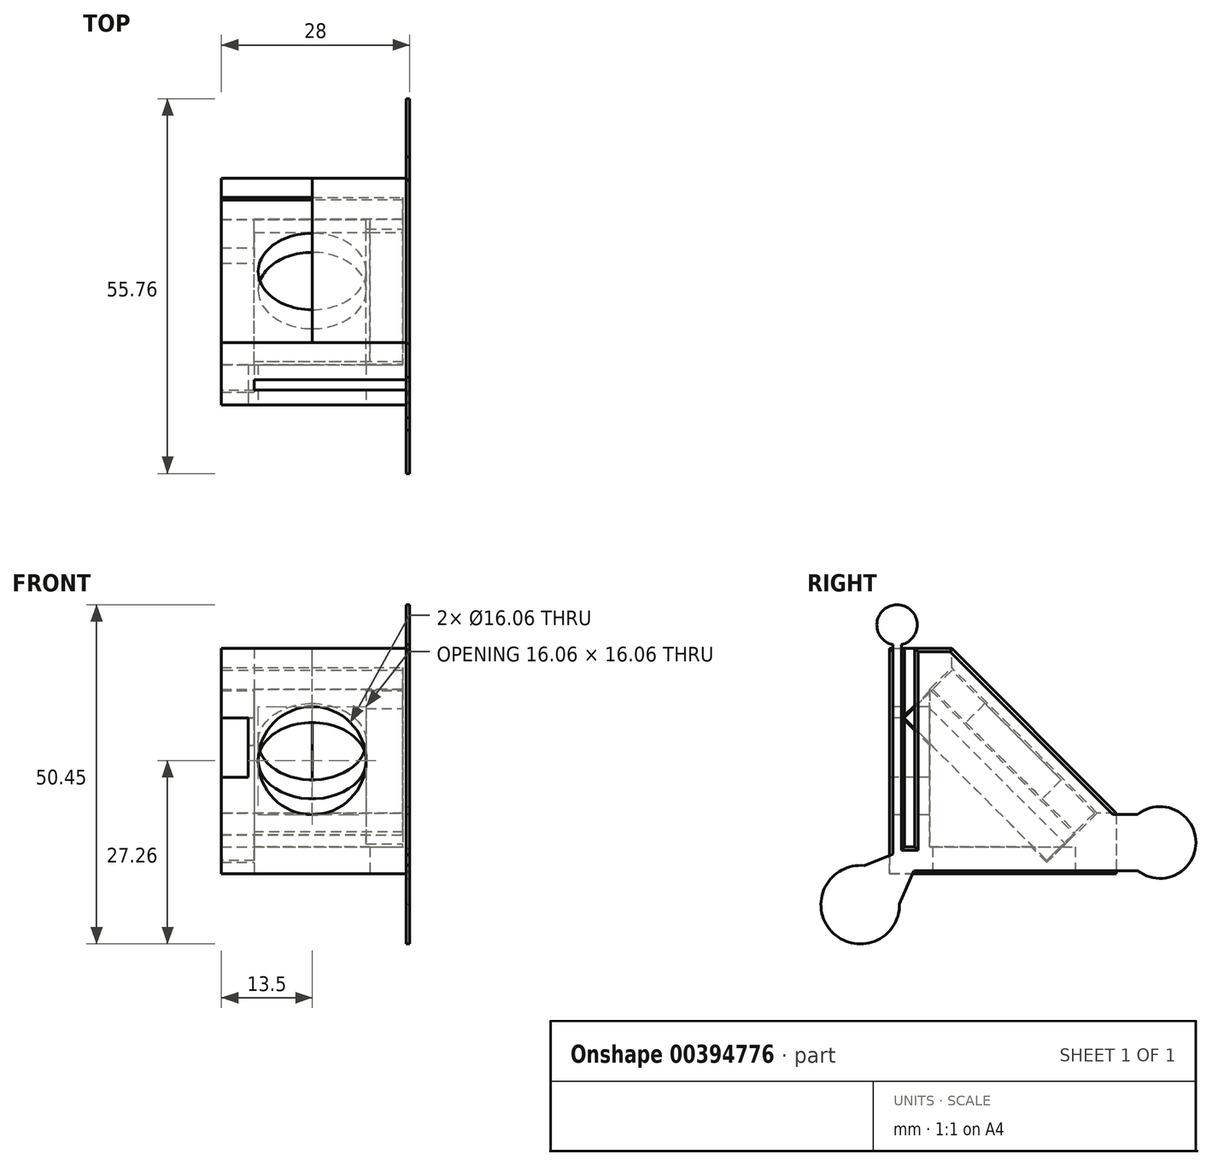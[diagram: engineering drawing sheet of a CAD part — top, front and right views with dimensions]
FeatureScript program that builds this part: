
annotation { "Feature Type Name" : "Feature", "Feature Type Description" : "" }
export const myFeature = defineFeature(function(context is Context, id is Id, definition is map)
    precondition{}
    {
        {
            var Q0;
            Q0=qCreatedBy(makeId("Top.planeOp"),FACE);
            var sketch = newSketch(context, id + "F0", { "sketchPlane" : qUnion([Q0])});
            skLineSegment(sketch, "E0", {"start": v(-77.13, 0) * mm, "end": v(74.23, 0) * mm, "construction": true});
            skSolve(sketch);
        }
        {
            var Q0;
            Q0=sQuery(id+"F0.wireOp",EDGE,"E0");
            cPlane(context, id + "F1", {"entities" : qUnion([Q0]), "cplaneType" : CPlaneType.LINE_ANGLE, "offset" : 25 * mm, "angle" : 45 * degree, "width" : 150 * mm, "height" : 150 * mm});
        }
        {
            var Q0;
            Q0=qCreatedBy(id+"F1.planeOp",FACE);
            var sketch = newSketch(context, id + "F2", { "sketchPlane" : qUnion([Q0])});
            skLineSegment(sketch, "E1.bottom", {"start": v(-13.5, -15) * mm, "end": v(13.5, -15) * mm});
            skLineSegment(sketch, "E1.top", {"start": v(-13.5, 15) * mm, "end": v(13.5, 15) * mm});
            skLineSegment(sketch, "E1.left", {"start": v(-13.5, -15) * mm, "end": v(-13.5, 15) * mm});
            skLineSegment(sketch, "E1.right", {"start": v(13.5, -15) * mm, "end": v(13.5, 15) * mm});
            skPoint(sketch, "E1.middle", {"position": v(0, 0) * mm});
            skLineSegment(sketch, "E2", {"start": v(13.5, 0) * mm, "end": v(8.6, 0) * mm, "construction": true});
            skPoint(sketch, "E2.endSnap0", {"position": v(13.5, 0) * mm});
            skLineSegment(sketch, "E3", {"start": v(-13.5, 0) * mm, "end": v(-8.03, 0) * mm, "construction": true});
            skPoint(sketch, "E3.endSnap0", {"position": v(-13.5, 0) * mm});
            skLineSegment(sketch, "E4", {"start": v(8.6, 15) * mm, "end": v(8.6, -15) * mm});
            skCircle(sketch, "E5", {"center": v(0, 0) * mm, "radius": 8.03 * mm});
            skSolve(sketch);
        }
        {
            var Q0;
            {var subQ1=sQuery(id+"F2.wireOp",EDGE,"E1.left");Q0=makeQuery(id+"F2.imprint","IMPRINT",FACE,{"disambiguationData":[TD([[makeQuery(id+"F2.imprint","IMPRINT",EDGE,{"derivedFrom":subQ1}),-1.0]])]});}
            var Q1;
            {var subQ0=sQuery(id+"F2.wireOp",EDGE,"E1.right");Q1=makeQuery(id+"F2.imprint","IMPRINT",FACE,{"disambiguationData":[TD([[makeQuery(id+"F2.imprint","IMPRINT",EDGE,{"derivedFrom":subQ0}),1.0]])]});}
            extrude(context, id + "F3", {"entities" : qUnion([Q0, Q1]), "depth" : 4 * mm});
        }
        {
            var Q0;
            {var subQ0=sQuery(id+"F2.wireOp",EDGE,"E1.right");Q0=makeQuery(id+"F2.imprint","IMPRINT",FACE,{"disambiguationData":[TD([[makeQuery(id+"F2.imprint","IMPRINT",EDGE,{"derivedFrom":subQ0}),1.0]])]});}
            extrude(context, id + "F4", {"entities" : qUnion([Q0]), "operationType" : NewBodyOperationType.ADD, "oppositeDirection" : true, "depth" : 6 * mm});
        }
        {
            var Q0;
            Q0=makeQuery(id+"F3.opExtrude","SWEPT_FACE",FACE,{"disambiguationData":[OSD([sQuery(id+"F2.wireOp",EDGE,"E1.left")])]});
            var sketch = newSketch(context, id + "F5", { "sketchPlane" : qUnion([Q0])});
            skLineSegment(sketch, "E6.0.0", {"start": v(-10.6, 10.6) * mm, "end": v(10.6, -10.6) * mm, "construction": true});
            skLineSegment(sketch, "E6.0.1", {"start": v(10.6, -10.6) * mm, "end": v(13.44, -7.78) * mm, "construction": true});
            skLineSegment(sketch, "E6.0.2", {"start": v(13.44, -7.78) * mm, "end": v(-7.78, 13.44) * mm, "construction": true});
            skLineSegment(sketch, "E6.0.3", {"start": v(-7.78, 13.44) * mm, "end": v(-10.6, 10.6) * mm, "construction": true});
            skLineSegment(sketch, "E7.0", {"start": v(13.86, -7.78) * mm, "end": v(-7.78, 13.86) * mm});
            skLineSegment(sketch, "E7.1", {"start": v(10.6, -11.03) * mm, "end": v(13.86, -7.78) * mm});
            skLineSegment(sketch, "E7.2", {"start": v(-11.03, 10.6) * mm, "end": v(10.6, -11.03) * mm});
            skLineSegment(sketch, "E7.3", {"start": v(-7.78, 13.86) * mm, "end": v(-11.03, 10.6) * mm});
            skLineSegment(sketch, "E8.0", {"start": v(16.69, -7.78) * mm, "end": v(-7.78, 16.69) * mm});
            skLineSegment(sketch, "E8.1", {"start": v(10.6, -13.86) * mm, "end": v(16.69, -7.78) * mm});
            skLineSegment(sketch, "E8.2", {"start": v(-13.86, 10.6) * mm, "end": v(10.6, -13.86) * mm});
            skLineSegment(sketch, "E8.3", {"start": v(-7.78, 16.69) * mm, "end": v(-13.86, 10.6) * mm});
            skLineSegment(sketch, "E9", {"start": v(-7.78, 16.69) * mm, "end": v(-13.86, 16.69) * mm});
            skPoint(sketch, "E10.0", {"position": v(6.36, -14.85) * mm});
            skLineSegment(sketch, "E11", {"start": v(10.6, -13.86) * mm, "end": v(10.6, -14.85) * mm, "construction": true});
            skLineSegment(sketch, "E12", {"start": v(-11.03, 10.6) * mm, "end": v(-17.03, 10.6) * mm, "construction": true});
            skLineSegment(sketch, "E13", {"start": v(-17.03, 10.6) * mm, "end": v(-17.03, 16.69) * mm});
            skLineSegment(sketch, "E14", {"start": v(-17.03, 16.69) * mm, "end": v(-13.86, 16.69) * mm});
            skLineSegment(sketch, "E15", {"start": v(-17.03, 10.6) * mm, "end": v(-17.03, -14.85) * mm});
            skLineSegment(sketch, "E16", {"start": v(0, -14.85) * mm, "end": v(0, -12.85) * mm, "construction": true});
            skLineSegment(sketch, "E17", {"start": v(-11.03, 10.6) * mm, "end": v(-11.03, -12.85) * mm});
            skLineSegment(sketch, "E18", {"start": v(-11.03, -12.85) * mm, "end": v(9.6, -12.85) * mm});
            skPoint(sketch, "E19.0", {"position": v(-14.85, 6.36) * mm});
            skLineSegment(sketch, "E20", {"start": v(6.36, -14.85) * mm, "end": v(6.36, -16.85) * mm, "construction": true});
            skLineSegment(sketch, "E21", {"start": v(-17.03, -14.85) * mm, "end": v(-17.03, -16.85) * mm});
            skLineSegment(sketch, "E22", {"start": v(-17.03, -16.85) * mm, "end": v(16.69, -16.85) * mm});
            skLineSegment(sketch, "E23", {"start": v(16.69, -16.85) * mm, "end": v(16.69, -7.78) * mm});
            skLineSegment(sketch, "E24.0", {"start": v(-14.85, 6.36) * mm, "end": v(-10.6, 10.6) * mm, "construction": true});
            skLineSegment(sketch, "E25.0", {"start": v(-14.85, 6.36) * mm, "end": v(6.36, -14.85) * mm, "construction": true});
            skLineSegment(sketch, "E26.0", {"start": v(6.36, -14.85) * mm, "end": v(10.6, -10.6) * mm, "construction": true});
            skLineSegment(sketch, "E27.1", {"start": v(-15.13, 6.36) * mm, "end": v(6.36, -15.13) * mm});
            skLineSegment(sketch, "E28", {"start": v(6.36, -15.13) * mm, "end": v(10.54, -10.96) * mm});
            skLineSegment(sketch, "E29", {"start": v(-15.13, 6.36) * mm, "end": v(-10.94, 10.51) * mm});
            skLineSegment(sketch, "E30", {"start": v(-7.78, 13.86) * mm, "end": v(-7.78, 16.69) * mm});
            skLineSegment(sketch, "E31", {"start": v(13.86, -7.78) * mm, "end": v(16.69, -7.78) * mm});
            skSolve(sketch);
        }
        {
            var Q0;
            Q0=makeQuery(id+"F5.imprint","IMPRINT",FACE,{"disambiguationData":[TD([[makeQuery(id+"F5.imprint","IMPRINT",EDGE,{"derivedFrom":sQuery(id+"F5.wireOp",EDGE,"E7.0")}),-1.0]])]});
            extrude(context, id + "F6", {"entities" : qUnion([Q0]), "oppositeDirection" : true, "depth" : 13.5 * mm});
        }
        {
            var Q0;
            {var subQ1=sQuery(id+"F5.wireOp",EDGE,"E7.3");Q0=makeQuery(id+"F5.imprint","IMPRINT",FACE,{"disambiguationData":[TD([[makeQuery(id+"F5.imprint","IMPRINT",EDGE,{"derivedFrom":subQ1}),-1.0]])]});}
            var Q1;
            {var subQ6=sQuery(id+"F5.wireOp",EDGE,"E8.1");Q1=makeQuery(id+"F5.imprint","IMPRINT",FACE,{"disambiguationData":[TD([[makeQuery(id+"F5.imprint","IMPRINT",EDGE,{"derivedFrom":subQ6}),-1.0]])]});}
            var Q2;
            {var subQ2=sQuery(id+"F5.wireOp",EDGE,"E7.1");Q2=makeQuery(id+"F5.imprint","IMPRINT",FACE,{"disambiguationData":[TD([[makeQuery(id+"F5.imprint","IMPRINT",EDGE,{"derivedFrom":subQ2}),-1.0]])]});}
            var Q3;
            {var subQ0=sQuery(id+"F5.wireOp",EDGE,"E18");var subQ1=sQuery(id+"F5.wireOp",EDGE,"E8.2");var subQ2=makeQuery(id+"F5.imprint","INTERSECT",VERTEX,{"derivedFrom":[subQ1,subQ0]});Q3=makeQuery(id+"F5.imprint","IMPRINT",FACE,{"disambiguationData":[TD([[makeQuery(id+"F5.imprint","IMPRINT",EDGE,{"disambiguationData":[TD([[subQ2,1.0]])],"derivedFrom":subQ1}),-1.0]])]});}
            var Q4;
            {var subQ0=sQuery(id+"F2.wireOp",EDGE,"E1.right");Q4=makeQuery(id+"F4.boolean.opBoolean","MERGE",FACE,{"derivedFrom":[makeQuery(id+"F3.opExtrude","SWEPT_FACE",FACE,{"disambiguationData":[OSD([subQ0])]}),makeQuery(id+"F4.opExtrude","SWEPT_FACE",FACE,{"disambiguationData":[OSD([subQ0])]})]});}
            extrude(context, id + "F7", {"entities" : qUnion([Q0, Q1, Q2, Q3]), "operationType" : NewBodyOperationType.ADD, "endBound" : BoundingType.UP_TO_SURFACE, "oppositeDirection" : true, "endBoundEntityFace" : qUnion([Q4]), "depth" : 25 * mm});
        }
        {
            var Q0;
            {var subQ0=sQuery(id+"F5.wireOp",EDGE,"E29");var subQ1=sQuery(id+"F5.wireOp",EDGE,"E8.2");var subQ2=makeQuery(id+"F5.imprint","INTERSECT",VERTEX,{"derivedFrom":[subQ1,subQ0]});Q0=makeQuery(id+"F5.imprint","IMPRINT",FACE,{"disambiguationData":[TD([[makeQuery(id+"F5.imprint","IMPRINT",EDGE,{"disambiguationData":[TD([[subQ2,-1.0]])],"derivedFrom":subQ1}),1.0]])]});}
            var Q1;
            {var subQ0=sQuery(id+"F5.wireOp",EDGE,"E29");var subQ1=sQuery(id+"F5.wireOp",EDGE,"E8.2");var subQ2=makeQuery(id+"F5.imprint","INTERSECT",VERTEX,{"derivedFrom":[subQ1,subQ0]});Q1=makeQuery(id+"F5.imprint","IMPRINT",FACE,{"disambiguationData":[TD([[makeQuery(id+"F5.imprint","IMPRINT",EDGE,{"disambiguationData":[TD([[subQ2,-1.0]])],"derivedFrom":subQ1}),-1.0]])]});}
            var Q2;
            {var subQ0=sQuery(id+"F5.wireOp",EDGE,"E27.1");var subQ1=sQuery(id+"F5.wireOp",EDGE,"E18");var subQ2=makeQuery(id+"F5.imprint","INTERSECT",VERTEX,{"derivedFrom":[subQ1,subQ0]});Q2=makeQuery(id+"F5.imprint","IMPRINT",FACE,{"disambiguationData":[TD([[makeQuery(id+"F5.imprint","IMPRINT",EDGE,{"disambiguationData":[TD([[subQ2,-1.0]])],"derivedFrom":subQ1}),-1.0]])]});}
            var Q3;
            Q3=makeQuery(id+"F4.opExtrude","SWEPT_FACE",FACE,{"disambiguationData":[OSD([sQuery(id+"F2.wireOp",EDGE,"E4")])]});
            extrude(context, id + "F8", {"entities" : qUnion([Q0, Q1, Q2]), "operationType" : NewBodyOperationType.ADD, "endBound" : BoundingType.UP_TO_SURFACE, "oppositeDirection" : true, "endBoundEntityFace" : qUnion([Q3]), "depth" : 25 * mm});
        }
        {
            var Q0;
            {var subQ5=sQuery(id+"F5.wireOp",EDGE,"E28");var subQ7=sQuery(id+"F5.wireOp",EDGE,"E7.2");var subQ8=makeQuery(id+"F5.imprint","INTERSECT",VERTEX,{"derivedFrom":[subQ7,subQ5]});Q0=makeQuery(id+"F5.imprint","IMPRINT",FACE,{"disambiguationData":[TD([[makeQuery(id+"F5.imprint","IMPRINT",EDGE,{"disambiguationData":[TD([[subQ8,1.0]])],"derivedFrom":subQ7}),-1.0]])]});}
            var Q1;
            Q1=sQuery(id+"F2.wireOp",VERTEX,"E3.end");
            extrude(context, id + "F9", {"entities" : qUnion([Q0]), "operationType" : NewBodyOperationType.ADD, "endBound" : BoundingType.UP_TO_VERTEX, "oppositeDirection" : true, "endBoundEntityVertex" : qUnion([Q1]), "depth" : 25 * mm});
        }
        {
            var Q0;
            Q0=makeQuery(id+"F7.opExtrude","SWEPT_FACE",FACE,{"disambiguationData":[OSD([sQuery(id+"F5.wireOp",EDGE,"E13"),sQuery(id+"F5.wireOp",EDGE,"E15"),sQuery(id+"F5.wireOp",EDGE,"E21")])]});
            var sketch = newSketch(context, id + "F10", { "sketchPlane" : qUnion([Q0])});
            skPoint(sketch, "E32.0", {"position": v(8.03, 0) * mm});
            skCircle(sketch, "E33", {"center": v(0, 0) * mm, "radius": 8.03 * mm});
            skSolve(sketch);
        }
        {
            var Q0;
            Q0=makeQuery(id+"F10.imprint","IMPRINT",FACE,{"disambiguationData":[TD([[makeQuery(id+"F10.imprint","IMPRINT",EDGE,{"derivedFrom":sQuery(id+"F10.wireOp",EDGE,"E33")}),1.0]])]});
            extrude(context, id + "F11", {"entities" : qUnion([Q0]), "operationType" : NewBodyOperationType.REMOVE, "oppositeDirection" : true, "depth" : 6 * mm});
        }
        {
            var Q0;
            {var subQ6=sQuery(id+"F5.wireOp",EDGE,"E8.1");Q0=makeQuery(id+"F5.imprint","IMPRINT",FACE,{"disambiguationData":[TD([[makeQuery(id+"F5.imprint","IMPRINT",EDGE,{"derivedFrom":subQ6}),-1.0]])]});}
            var sketch = newSketch(context, id + "F12", { "sketchPlane" : qUnion([Q0])});
            skPoint(sketch, "E34.0", {"position": v(-17.03, 16.69) * mm});
            skLineSegment(sketch, "E35", {"start": v(-17.03, 16.69) * mm, "end": v(-14.03, 16.69) * mm, "construction": true});
            skPoint(sketch, "E36.0", {"position": v(-11.03, -12.85) * mm});
            skLineSegment(sketch, "E37.bottom", {"start": v(-13.28, -12.85) * mm, "end": v(-14.78, -12.85) * mm});
            skLineSegment(sketch, "E37.left", {"start": v(-13.28, -12.85) * mm, "end": v(-13.28, 16.69) * mm});
            skLineSegment(sketch, "E37.right", {"start": v(-14.78, -12.85) * mm, "end": v(-14.78, 16.69) * mm});
            skPoint(sketch, "E37.middle", {"position": v(-14.03, 16.69) * mm});
            skLineSegment(sketch, "E38", {"start": v(-14.78, 16.69) * mm, "end": v(-13.28, 16.69) * mm});
            skSolve(sketch);
        }
        {
            var Q0;
            {var subQ0=sQuery(id+"F12.wireOp",EDGE,"E38");var subQ2=sQuery(id+"F12.wireOp",EDGE,"E37.right");var subQ3=makeQuery(id+"F12.imprint","INTERSECT",VERTEX,{"derivedFrom":[makeQuery(id+"F5.imprint","IMPRINT",EDGE,{"derivedFrom":sQuery(id+"F5.wireOp",EDGE,"E14")}),subQ2,subQ0]});Q0=makeQuery(id+"F12.imprint","IMPRINT",FACE,{"disambiguationData":[TD([[makeQuery(id+"F12.imprint","IMPRINT",EDGE,{"disambiguationData":[TD([[subQ3,-1.0]])],"derivedFrom":subQ0}),-1.0]])]});}
            var Q1;
            {var subQ0=sQuery(id+"F12.wireOp",EDGE,"E37.left");var subQ1=sQuery(id+"F5.wireOp",EDGE,"E8.3");var subQ5=makeQuery(id+"F5.imprint","IMPRINT",EDGE,{"derivedFrom":subQ1});var subQ6=makeQuery(id+"F12.imprint","INTERSECT",VERTEX,{"derivedFrom":[subQ5,subQ0]});Q1=makeQuery(id+"F12.imprint","IMPRINT",FACE,{"disambiguationData":[TD([[makeQuery(id+"F12.imprint","IMPRINT",EDGE,{"disambiguationData":[TD([[subQ6,1.0]])],"derivedFrom":subQ0}),1.0]])]});}
            var Q2;
            {var subQ0=sQuery(id+"F12.wireOp",EDGE,"E37.left");var subQ1=sQuery(id+"F5.wireOp",EDGE,"E29");var subQ2=sQuery(id+"F5.wireOp",EDGE,"E27.1");var subQ3=makeQuery(id+"F5.imprint","INTERSECT",VERTEX,{"derivedFrom":[subQ2,subQ1]});var subQ4=makeQuery(id+"F5.imprint","IMPRINT",EDGE,{"disambiguationData":[TD([[subQ3,-1.0]])],"derivedFrom":subQ2});var subQ5=makeQuery(id+"F12.imprint","INTERSECT",VERTEX,{"derivedFrom":[subQ4,subQ0]});Q2=makeQuery(id+"F12.imprint","IMPRINT",FACE,{"disambiguationData":[TD([[makeQuery(id+"F12.imprint","IMPRINT",EDGE,{"disambiguationData":[TD([[subQ5,-1.0]])],"derivedFrom":subQ0}),1.0]])]});}
            var Q3;
            {var subQ0=sQuery(id+"F12.wireOp",EDGE,"E37.bottom");Q3=makeQuery(id+"F12.imprint","IMPRINT",FACE,{"disambiguationData":[TD([[makeQuery(id+"F12.imprint","IMPRINT",EDGE,{"derivedFrom":subQ0}),-1.0]])]});}
            var Q4;
            Q4=makeQuery(id+"F4.opExtrude","SWEPT_FACE",FACE,{"disambiguationData":[OSD([sQuery(id+"F2.wireOp",EDGE,"E4")])]});
            extrude(context, id + "F13", {"entities" : qUnion([Q0, Q1, Q2, Q3]), "operationType" : NewBodyOperationType.REMOVE, "endBound" : BoundingType.UP_TO_SURFACE, "oppositeDirection" : true, "endBoundEntityFace" : qUnion([Q4]), "depth" : 25 * mm});
        }
        {
            var Q0;
            Q0=makeQuery(id+"F7.opExtrude","CAP_FACE",FACE,{"disambiguationData":[OSD([sQuery(id+"F5.wireOp",EDGE,"E7.1"),sQuery(id+"F5.wireOp",EDGE,"E7.2"),sQuery(id+"F5.wireOp",EDGE,"E7.3"),sQuery(id+"F5.wireOp",EDGE,"E9"),sQuery(id+"F5.wireOp",EDGE,"E13"),sQuery(id+"F5.wireOp",EDGE,"E14"),sQuery(id+"F5.wireOp",EDGE,"E15"),sQuery(id+"F5.wireOp",EDGE,"E17"),sQuery(id+"F5.wireOp",EDGE,"E18"),sQuery(id+"F5.wireOp",EDGE,"E21"),sQuery(id+"F5.wireOp",EDGE,"E22"),sQuery(id+"F5.wireOp",EDGE,"E23"),sQuery(id+"F5.wireOp",EDGE,"E27.1"),sQuery(id+"F5.wireOp",EDGE,"E28"),sQuery(id+"F5.wireOp",EDGE,"E29"),sQuery(id+"F5.wireOp",EDGE,"E30"),sQuery(id+"F5.wireOp",EDGE,"E31")])],"isStart":false});
            var sketch = newSketch(context, id + "F14", { "sketchPlane" : qUnion([Q0])});
            skLineSegment(sketch, "E39.0.0", {"start": v(11.03, 2.26) * mm, "end": v(11.03, -12.85) * mm, "construction": true});
            skLineSegment(sketch, "E39.0.1", {"start": v(11.03, -12.85) * mm, "end": v(-4.08, -12.85) * mm, "construction": true});
            skLineSegment(sketch, "E39.0.2", {"start": v(-4.08, -12.85) * mm, "end": v(-6.36, -15.13) * mm, "construction": true});
            skLineSegment(sketch, "E39.0.3", {"start": v(-6.36, -15.13) * mm, "end": v(-10.54, -10.96) * mm, "construction": true});
            skLineSegment(sketch, "E39.0.4", {"start": v(-10.54, -10.96) * mm, "end": v(-10.6, -11.03) * mm, "construction": true});
            skLineSegment(sketch, "E39.0.5", {"start": v(-10.6, -11.03) * mm, "end": v(-13.86, -7.78) * mm, "construction": true});
            skLineSegment(sketch, "E39.0.6", {"start": v(-13.86, -7.78) * mm, "end": v(-16.69, -7.78) * mm, "construction": true});
            skLineSegment(sketch, "E39.0.7", {"start": v(-16.69, -7.78) * mm, "end": v(-16.69, -16.85) * mm, "construction": true});
            skLineSegment(sketch, "E39.0.8", {"start": v(-16.69, -16.85) * mm, "end": v(17.03, -16.85) * mm, "construction": true});
            skLineSegment(sketch, "E39.0.9", {"start": v(17.03, -16.85) * mm, "end": v(17.03, 16.69) * mm, "construction": true});
            skLineSegment(sketch, "E39.0.10", {"start": v(17.03, 16.69) * mm, "end": v(7.78, 16.69) * mm, "construction": true});
            skLineSegment(sketch, "E39.0.11", {"start": v(7.78, 16.69) * mm, "end": v(7.78, 13.86) * mm, "construction": true});
            skLineSegment(sketch, "E39.0.12", {"start": v(7.78, 13.86) * mm, "end": v(11.03, 10.6) * mm, "construction": true});
            skLineSegment(sketch, "E39.0.13", {"start": v(11.03, 10.6) * mm, "end": v(11.03, 10.42) * mm, "construction": true});
            skLineSegment(sketch, "E39.0.14", {"start": v(11.03, 10.42) * mm, "end": v(15.13, 6.36) * mm, "construction": true});
            skLineSegment(sketch, "E39.0.15", {"start": v(15.13, 6.36) * mm, "end": v(11.03, 2.26) * mm, "construction": true});
            skLineSegment(sketch, "E40", {"start": v(15.13, 6.36) * mm, "end": v(17.03, 6.36) * mm});
            skLineSegment(sketch, "E41", {"start": v(15.13, 6.36) * mm, "end": v(11.03, 2.26) * mm});
            skLineSegment(sketch, "E42", {"start": v(11.03, 2.26) * mm, "end": v(11.03, -2.47) * mm});
            skLineSegment(sketch, "E43", {"start": v(11.03, -2.47) * mm, "end": v(17.03, -2.47) * mm});
            skLineSegment(sketch, "E44", {"start": v(17.03, -2.47) * mm, "end": v(17.03, 6.36) * mm});
            skSolve(sketch);
        }
        {
            var Q0;
            Q0=makeQuery(id+"F14.imprint","IMPRINT",FACE,{"disambiguationData":[TD([[makeQuery(id+"F14.imprint","IMPRINT",EDGE,{"derivedFrom":sQuery(id+"F14.wireOp",EDGE,"E40")}),-1.0]])]});
            extrude(context, id + "F15", {"entities" : qUnion([Q0]), "operationType" : NewBodyOperationType.REMOVE, "oppositeDirection" : true, "depth" : 4 * mm});
        }
        {
            var Q0;
            {var subQ0=sQuery(id+"F5.wireOp",EDGE,"E29");var subQ1=sQuery(id+"F5.wireOp",EDGE,"E8.2");var subQ2=makeQuery(id+"F5.imprint","INTERSECT",VERTEX,{"derivedFrom":[subQ1,subQ0]});Q0=makeQuery(id+"F5.imprint","IMPRINT",FACE,{"disambiguationData":[TD([[makeQuery(id+"F5.imprint","IMPRINT",EDGE,{"disambiguationData":[TD([[subQ2,-1.0]])],"derivedFrom":subQ1}),-1.0]])]});}
            var Q1;
            {var subQ1=sQuery(id+"F5.wireOp",EDGE,"E7.3");Q1=makeQuery(id+"F5.imprint","IMPRINT",FACE,{"disambiguationData":[TD([[makeQuery(id+"F5.imprint","IMPRINT",EDGE,{"derivedFrom":subQ1}),-1.0]])]});}
            var Q2;
            {var subQ6=sQuery(id+"F5.wireOp",EDGE,"E8.1");Q2=makeQuery(id+"F5.imprint","IMPRINT",FACE,{"disambiguationData":[TD([[makeQuery(id+"F5.imprint","IMPRINT",EDGE,{"derivedFrom":subQ6}),-1.0]])]});}
            var Q3;
            {var subQ0=sQuery(id+"F5.wireOp",EDGE,"E18");var subQ1=sQuery(id+"F5.wireOp",EDGE,"E17");var subQ2=makeQuery(id+"F5.imprint","INTERSECT",VERTEX,{"derivedFrom":[subQ1,subQ0]});Q3=makeQuery(id+"F5.imprint","IMPRINT",FACE,{"disambiguationData":[TD([[makeQuery(id+"F5.imprint","IMPRINT",EDGE,{"disambiguationData":[TD([[subQ2,1.0]])],"derivedFrom":subQ1}),1.0]])]});}
            var Q4;
            {var subQ0=sQuery(id+"F5.wireOp",EDGE,"E29");var subQ1=sQuery(id+"F5.wireOp",EDGE,"E8.2");var subQ2=makeQuery(id+"F5.imprint","INTERSECT",VERTEX,{"derivedFrom":[subQ1,subQ0]});Q4=makeQuery(id+"F5.imprint","IMPRINT",FACE,{"disambiguationData":[TD([[makeQuery(id+"F5.imprint","IMPRINT",EDGE,{"disambiguationData":[TD([[subQ2,-1.0]])],"derivedFrom":subQ1}),1.0]])]});}
            var Q5;
            {var subQ1=sQuery(id+"F5.wireOp",EDGE,"E17");var subQ7=sQuery(id+"F5.wireOp",EDGE,"E8.2");var subQ8=makeQuery(id+"F5.imprint","INTERSECT",VERTEX,{"derivedFrom":[subQ7,subQ1]});Q5=makeQuery(id+"F5.imprint","IMPRINT",FACE,{"disambiguationData":[TD([[makeQuery(id+"F5.imprint","IMPRINT",EDGE,{"disambiguationData":[TD([[subQ8,-1.0]])],"derivedFrom":subQ7}),-1.0]])]});}
            var Q6;
            {var subQ5=sQuery(id+"F5.wireOp",EDGE,"E28");var subQ7=sQuery(id+"F5.wireOp",EDGE,"E7.2");var subQ8=makeQuery(id+"F5.imprint","INTERSECT",VERTEX,{"derivedFrom":[subQ7,subQ5]});Q6=makeQuery(id+"F5.imprint","IMPRINT",FACE,{"disambiguationData":[TD([[makeQuery(id+"F5.imprint","IMPRINT",EDGE,{"disambiguationData":[TD([[subQ8,1.0]])],"derivedFrom":subQ7}),-1.0]])]});}
            var Q7;
            Q7=makeQuery(id+"F5.imprint","IMPRINT",FACE,{"disambiguationData":[TD([[makeQuery(id+"F5.imprint","IMPRINT",EDGE,{"derivedFrom":sQuery(id+"F5.wireOp",EDGE,"E7.0")}),1.0]])]});
            var Q8;
            Q8=makeQuery(id+"F5.imprint","IMPRINT",FACE,{"disambiguationData":[TD([[makeQuery(id+"F5.imprint","IMPRINT",EDGE,{"derivedFrom":sQuery(id+"F5.wireOp",EDGE,"E7.0")}),-1.0]])]});
            var Q9;
            {var subQ0=sQuery(id+"F5.wireOp",EDGE,"E27.1");var subQ1=sQuery(id+"F5.wireOp",EDGE,"E18");var subQ2=makeQuery(id+"F5.imprint","INTERSECT",VERTEX,{"derivedFrom":[subQ1,subQ0]});Q9=makeQuery(id+"F5.imprint","IMPRINT",FACE,{"disambiguationData":[TD([[makeQuery(id+"F5.imprint","IMPRINT",EDGE,{"disambiguationData":[TD([[subQ2,-1.0]])],"derivedFrom":subQ1}),-1.0]])]});}
            var Q10;
            {var subQ2=sQuery(id+"F5.wireOp",EDGE,"E7.1");Q10=makeQuery(id+"F5.imprint","IMPRINT",FACE,{"disambiguationData":[TD([[makeQuery(id+"F5.imprint","IMPRINT",EDGE,{"derivedFrom":subQ2}),-1.0]])]});}
            var Q11;
            {var subQ0=sQuery(id+"F5.wireOp",EDGE,"E18");var subQ1=sQuery(id+"F5.wireOp",EDGE,"E8.2");var subQ2=makeQuery(id+"F5.imprint","INTERSECT",VERTEX,{"derivedFrom":[subQ1,subQ0]});Q11=makeQuery(id+"F5.imprint","IMPRINT",FACE,{"disambiguationData":[TD([[makeQuery(id+"F5.imprint","IMPRINT",EDGE,{"disambiguationData":[TD([[subQ2,1.0]])],"derivedFrom":subQ1}),-1.0]])]});}
            var Q12;
            {var subQ0=sQuery(id+"F2.wireOp",EDGE,"E1.left");Q12=makeQuery(id+"F5.imprint","IMPRINT",FACE,{"disambiguationData":[TD([[makeQuery(id+"F5.imprint","IMPRINT",EDGE,{"derivedFrom":makeQuery(id+"F3.opExtrude","CAP_EDGE",EDGE,{"disambiguationData":[OSD([subQ0])],"isStart":true})}),-1.0]])]});}
            var Q13;
            {var subQ1=sQuery(id+"F5.wireOp",EDGE,"E7.2");var subQ3=sQuery(id+"F5.wireOp",EDGE,"E29");var subQ4=makeQuery(id+"F5.imprint","INTERSECT",VERTEX,{"derivedFrom":[subQ1,subQ3]});Q13=makeQuery(id+"F5.imprint","IMPRINT",FACE,{"disambiguationData":[TD([[makeQuery(id+"F5.imprint","IMPRINT",EDGE,{"disambiguationData":[TD([[subQ4,1.0]])],"derivedFrom":subQ3}),1.0]])]});}
            extrude(context, id + "F16", {"entities" : qUnion([Q0, Q1, Q2, Q3, Q4, Q5, Q6, Q7, Q8, Q9, Q10, Q11, Q12, Q13]), "operationType" : NewBodyOperationType.ADD, "depth" : 1 * mm});
        }
        {
            var Q0;
            {var subQ0=sQuery(id+"F5.wireOp",EDGE,"E22");Q0=makeQuery(id+"F16.boolean.opBoolean","MERGE",FACE,{"derivedFrom":[makeQuery(id+"F7.opExtrude","SWEPT_FACE",FACE,{"disambiguationData":[OSD([subQ0])]}),makeQuery(id+"F16.opExtrude","SWEPT_FACE",FACE,{"disambiguationData":[OSD([subQ0])]})]});}
            var sketch = newSketch(context, id + "F17", { "sketchPlane" : qUnion([Q0])});
            skPoint(sketch, "E45.0", {"position": v(-8.6, -10.6) * mm});
            skLineSegment(sketch, "E46.bottom", {"start": v(-8.6, -10.6) * mm, "end": v(8.6, -10.6) * mm});
            skLineSegment(sketch, "E46.top", {"start": v(-8.6, 10.6) * mm, "end": v(8.6, 10.6) * mm});
            skLineSegment(sketch, "E46.left", {"start": v(-8.6, -10.6) * mm, "end": v(-8.6, 10.6) * mm});
            skLineSegment(sketch, "E46.right", {"start": v(8.6, -10.6) * mm, "end": v(8.6, 10.6) * mm});
            skPoint(sketch, "E46.middle", {"position": v(0, 0) * mm});
            skSolve(sketch);
        }
        {
            var Q0;
            Q0=makeQuery(id+"F17.imprint","IMPRINT",FACE,{"disambiguationData":[TD([[makeQuery(id+"F17.imprint","IMPRINT",EDGE,{"derivedFrom":sQuery(id+"F17.wireOp",EDGE,"E46.bottom")}),1.0]])]});
            var Q1;
            {var subQ0=sQuery(id+"F5.wireOp",EDGE,"E18");Q1=makeQuery(id+"F8.boolean.opBoolean","MERGE",FACE,{"derivedFrom":[makeQuery(id+"F7.opExtrude","SWEPT_FACE",FACE,{"disambiguationData":[OSD([subQ0])]}),makeQuery(id+"F8.opExtrude","SWEPT_FACE",FACE,{"disambiguationData":[OSD([subQ0])]})]});}
            extrude(context, id + "F18", {"entities" : qUnion([Q0]), "operationType" : NewBodyOperationType.REMOVE, "endBound" : BoundingType.UP_TO_SURFACE, "oppositeDirection" : true, "endBoundEntityFace" : qUnion([Q1]), "depth" : 25 * mm});
        }
        {
            var Q0;
            Q0=makeQuery(id+"F16.opExtrude","CAP_FACE",FACE,{"disambiguationData":[OSD([sQuery(id+"F5.wireOp",EDGE,"E8.0"),sQuery(id+"F5.wireOp",EDGE,"E9"),sQuery(id+"F5.wireOp",EDGE,"E13"),sQuery(id+"F5.wireOp",EDGE,"E14"),sQuery(id+"F5.wireOp",EDGE,"E15"),sQuery(id+"F5.wireOp",EDGE,"E21"),sQuery(id+"F5.wireOp",EDGE,"E22"),sQuery(id+"F5.wireOp",EDGE,"E23")])],"isStart":false});
            var sketch = newSketch(context, id + "F19", { "sketchPlane" : qUnion([Q0])});
            skLineSegment(sketch, "E47.0", {"start": v(-14.78, 16.69) * mm, "end": v(-13.28, 16.69) * mm});
            skLineSegment(sketch, "E48.0", {"start": v(-13.28, -12.85) * mm, "end": v(-13.28, 16.69) * mm});
            skLineSegment(sketch, "E49.0", {"start": v(-14.78, -12.85) * mm, "end": v(-14.78, 16.69) * mm});
            skLineSegment(sketch, "E50.0", {"start": v(-13.28, -12.85) * mm, "end": v(-14.78, -12.85) * mm});
            skSolve(sketch);
        }
        {
            var Q0;
            {var subQ0=sQuery(id+"F19.wireOp",EDGE,"E50.0");Q0=makeQuery(id+"F19.imprint","IMPRINT",FACE,{"disambiguationData":[TD([[makeQuery(id+"F19.imprint","IMPRINT",EDGE,{"derivedFrom":subQ0}),-1.0]])]});}
            var Q1;
            {var subQ0=sQuery(id+"F5.wireOp",EDGE,"E14");var subQ1=sQuery(id+"F5.wireOp",EDGE,"E9");Q1=makeQuery(id+"F16.boolean.opBoolean","SPLIT",FACE,{"disambiguationData":[TD([makeQuery(id+"F13.boolean.opBoolean","COPY",FACE,{"derivedFrom":makeQuery(id+"F13.opExtrude","SWEPT_FACE",FACE,{"disambiguationData":[OSD([sQuery(id+"F12.wireOp",EDGE,"E37.bottom")])]})})])],"derivedFrom":makeQuery(id+"F16.opExtrude","CAP_FACE",FACE,{"disambiguationData":[OSD([sQuery(id+"F5.wireOp",EDGE,"E8.0"),subQ1,sQuery(id+"F5.wireOp",EDGE,"E13"),subQ0,sQuery(id+"F5.wireOp",EDGE,"E15"),sQuery(id+"F5.wireOp",EDGE,"E21"),sQuery(id+"F5.wireOp",EDGE,"E22"),sQuery(id+"F5.wireOp",EDGE,"E23")])],"isStart":true})});}
            extrude(context, id + "F20", {"entities" : qUnion([Q0]), "operationType" : NewBodyOperationType.REMOVE, "endBound" : BoundingType.UP_TO_SURFACE, "oppositeDirection" : true, "endBoundEntityFace" : qUnion([Q1]), "depth" : 25 * mm});
        }
        {
            var Q0;
            Q0=makeQuery(id+"F16.opExtrude","CAP_FACE",FACE,{"disambiguationData":[OSD([sQuery(id+"F5.wireOp",EDGE,"E8.0"),sQuery(id+"F5.wireOp",EDGE,"E9"),sQuery(id+"F5.wireOp",EDGE,"E13"),sQuery(id+"F5.wireOp",EDGE,"E14"),sQuery(id+"F5.wireOp",EDGE,"E15"),sQuery(id+"F5.wireOp",EDGE,"E21"),sQuery(id+"F5.wireOp",EDGE,"E22"),sQuery(id+"F5.wireOp",EDGE,"E23")])],"isStart":false});
            chamfer(context, id + "F21", {"entities" : qUnion([Q0]), "width" : .5 * mm, "tangentPropagation" : true});
        }
        {
            var Q0;
            Q0=makeQuery(id+"F16.opExtrude","CAP_FACE",FACE,{"disambiguationData":[OSD([sQuery(id+"F5.wireOp",EDGE,"E8.0"),sQuery(id+"F5.wireOp",EDGE,"E9"),sQuery(id+"F5.wireOp",EDGE,"E13"),sQuery(id+"F5.wireOp",EDGE,"E14"),sQuery(id+"F5.wireOp",EDGE,"E15"),sQuery(id+"F5.wireOp",EDGE,"E21"),sQuery(id+"F5.wireOp",EDGE,"E22"),sQuery(id+"F5.wireOp",EDGE,"E23")])],"isStart":false});
            var sketch = newSketch(context, id + "F22", { "sketchPlane" : qUnion([Q0])});
            skLineSegment(sketch, "E51", {"start": v(-15.9, 16.19) * mm, "end": v(-15.9, 20.19) * mm, "construction": true});
            skCircle(sketch, "E52", {"center": v(-15.9, 20.19) * mm, "radius": 3 * mm});
            skLineSegment(sketch, "E53", {"start": v(-16.53, 16.19) * mm, "end": v(-16.53, 17.25) * mm});
            skLineSegment(sketch, "E54", {"start": v(-15.28, 16.19) * mm, "end": v(-15.28, 17.25) * mm});
            skLineSegment(sketch, "E55", {"start": v(-16.53, 16.19) * mm, "end": v(-15.28, 16.19) * mm});
            skLineSegment(sketch, "E56", {"start": v(16.19, -12.17) * mm, "end": v(23.19, -12.17) * mm, "construction": true});
            skCircle(sketch, "E57", {"center": v(23.19, -12.17) * mm, "radius": 5.34 * mm});
            skLineSegment(sketch, "E58", {"start": v(16.19, -16.35) * mm, "end": v(19.86, -16.35) * mm});
            skLineSegment(sketch, "E59", {"start": v(16.19, -7.99) * mm, "end": v(19.86, -7.99) * mm});
            skLineSegment(sketch, "E60", {"start": v(-16.53, -16.35) * mm, "end": v(-21.38, -21.42) * mm, "construction": true});
            skCircle(sketch, "E61", {"center": v(-21.38, -21.42) * mm, "radius": 5.84 * mm});
            skLineSegment(sketch, "E62", {"start": v(-13.43, -16.35) * mm, "end": v(-15.54, -21.32) * mm});
            skLineSegment(sketch, "E63", {"start": v(-16.53, -13.87) * mm, "end": v(-20.77, -15.61) * mm});
            skSolve(sketch);
        }
        {
            var Q0;
            {var subQ0=sQuery(id+"F22.wireOp",EDGE,"E52");var subQ1=makeQuery(id+"F22.imprint","INTERSECT",VERTEX,{"derivedFrom":[subQ0,sQuery(id+"F22.wireOp",EDGE,"E53")]});Q0=makeQuery(id+"F22.imprint","IMPRINT",FACE,{"disambiguationData":[TD([[makeQuery(id+"F22.imprint","IMPRINT",EDGE,{"disambiguationData":[TD([[subQ1,-1.0]])],"derivedFrom":subQ0}),1.0]])]});}
            var Q1;
            {var subQ0=sQuery(id+"F22.wireOp",EDGE,"E53");Q1=makeQuery(id+"F22.imprint","IMPRINT",FACE,{"disambiguationData":[TD([[makeQuery(id+"F22.imprint","IMPRINT",EDGE,{"derivedFrom":subQ0}),-1.0]])]});}
            var Q2;
            {var subQ0=sQuery(id+"F22.wireOp",EDGE,"E61");var subQ1=makeQuery(id+"F22.imprint","INTERSECT",VERTEX,{"derivedFrom":[subQ0,sQuery(id+"F22.wireOp",EDGE,"E62")]});Q2=makeQuery(id+"F22.imprint","IMPRINT",FACE,{"disambiguationData":[TD([[makeQuery(id+"F22.imprint","IMPRINT",EDGE,{"disambiguationData":[TD([[subQ1,-1.0]])],"derivedFrom":subQ0}),1.0]])]});}
            var Q3;
            {var subQ9=sQuery(id+"F22.wireOp",EDGE,"E62");Q3=makeQuery(id+"F22.imprint","IMPRINT",FACE,{"disambiguationData":[TD([[makeQuery(id+"F22.imprint","IMPRINT",EDGE,{"derivedFrom":subQ9}),-1.0]])]});}
            var Q4;
            {var subQ0=sQuery(id+"F22.wireOp",EDGE,"E57");var subQ1=makeQuery(id+"F22.imprint","INTERSECT",VERTEX,{"derivedFrom":[subQ0,sQuery(id+"F22.wireOp",EDGE,"E58")]});Q4=makeQuery(id+"F22.imprint","IMPRINT",FACE,{"disambiguationData":[TD([[makeQuery(id+"F22.imprint","IMPRINT",EDGE,{"disambiguationData":[TD([[subQ1,1.0]])],"derivedFrom":subQ0}),1.0]])]});}
            var Q5;
            {var subQ0=sQuery(id+"F22.wireOp",EDGE,"E58");Q5=makeQuery(id+"F22.imprint","IMPRINT",FACE,{"disambiguationData":[TD([[makeQuery(id+"F22.imprint","IMPRINT",EDGE,{"derivedFrom":subQ0}),1.0]])]});}
            extrude(context, id + "F23", {"entities" : qUnion([Q0, Q1, Q2, Q3, Q4, Q5]), "operationType" : NewBodyOperationType.ADD, "oppositeDirection" : true, "depth" : .5 * mm});
        }
    });
